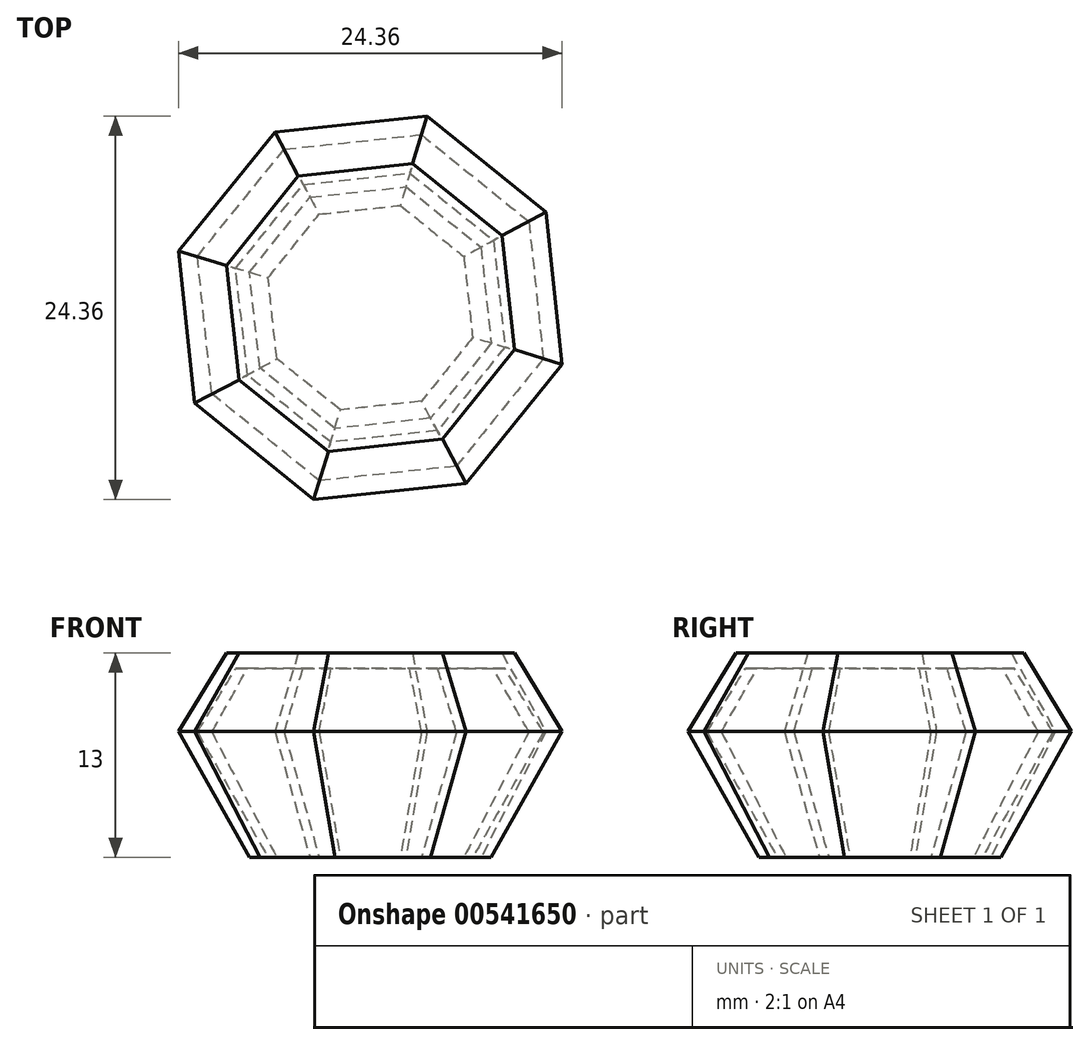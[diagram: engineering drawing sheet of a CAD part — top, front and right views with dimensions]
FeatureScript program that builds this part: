
annotation { "Feature Type Name" : "Feature", "Feature Type Description" : "" }
export const myFeature = defineFeature(function(context is Context, id is Id, definition is map)
    precondition{}
    {
        {
            var Q0;
            Q0=qCreatedBy(makeId("Top.planeOp"),FACE);
            var sketch = newSketch(context, id + "F0", { "sketchPlane" : qUnion([Q0])});
            skCircle(sketch, "E0.cCircle", {"center": v(0, 0) * mm, "radius": 9.53 * mm, "construction": true});
            skLineSegment(sketch, "E0.0", {"start": v(-4.58, 8.35) * mm, "end": v(2.67, 9.14) * mm});
            skLineSegment(sketch, "E0.1", {"start": v(2.67, 9.14) * mm, "end": v(8.35, 4.58) * mm});
            skLineSegment(sketch, "E0.2", {"start": v(8.35, 4.58) * mm, "end": v(9.14, -2.67) * mm});
            skLineSegment(sketch, "E0.3", {"start": v(9.14, -2.67) * mm, "end": v(4.58, -8.35) * mm});
            skLineSegment(sketch, "E0.4", {"start": v(4.58, -8.35) * mm, "end": v(-2.67, -9.14) * mm});
            skLineSegment(sketch, "E0.5", {"start": v(-2.67, -9.14) * mm, "end": v(-8.35, -4.58) * mm});
            skLineSegment(sketch, "E0.6", {"start": v(-8.35, -4.58) * mm, "end": v(-9.14, 2.67) * mm});
            skLineSegment(sketch, "E0.7", {"start": v(-9.14, 2.67) * mm, "end": v(-4.58, 8.35) * mm});
            skSolve(sketch);
        }
        {
            var Q0;
            Q0=qCreatedBy(makeId("Top.planeOp"),FACE);
            cPlane(context, id + "F1", {"entities" : qUnion([Q0]), "cplaneType" : CPlaneType.OFFSET, "offset" : 5 * mm, "oppositeDirection" : true, "width" : 152.4 * mm, "height" : 152.4 * mm});
        }
        {
            var Q0;
            Q0=qCreatedBy(id+"F1.planeOp",FACE);
            var sketch = newSketch(context, id + "F2", { "sketchPlane" : qUnion([Q0])});
            skCircle(sketch, "E1.cCircle", {"center": v(0, 0) * mm, "radius": 12.7 * mm, "construction": true});
            skLineSegment(sketch, "E1.0", {"start": v(-6.06, 11.16) * mm, "end": v(3.6, 12.18) * mm});
            skLineSegment(sketch, "E1.1", {"start": v(3.6, 12.18) * mm, "end": v(11.16, 6.06) * mm});
            skLineSegment(sketch, "E1.2", {"start": v(11.16, 6.06) * mm, "end": v(12.18, -3.6) * mm});
            skLineSegment(sketch, "E1.3", {"start": v(12.18, -3.6) * mm, "end": v(6.06, -11.16) * mm});
            skLineSegment(sketch, "E1.4", {"start": v(6.06, -11.16) * mm, "end": v(-3.6, -12.18) * mm});
            skLineSegment(sketch, "E1.5", {"start": v(-3.6, -12.18) * mm, "end": v(-11.16, -6.06) * mm});
            skLineSegment(sketch, "E1.6", {"start": v(-11.16, -6.06) * mm, "end": v(-12.18, 3.6) * mm});
            skLineSegment(sketch, "E1.7", {"start": v(-12.18, 3.6) * mm, "end": v(-6.06, 11.16) * mm});
            skSolve(sketch);
        }
        {
            var Q0;
            Q0=makeQuery(id+"F0.imprint","IMPRINT",FACE,{"disambiguationData":[TD([[makeQuery(id+"F0.imprint","IMPRINT",EDGE,{"derivedFrom":sQuery(id+"F0.wireOp",EDGE,"E0.0")}),-1.0]])]});
            var Q1;
            Q1=makeQuery(id+"F2.imprint","IMPRINT",FACE,{"disambiguationData":[TD([[makeQuery(id+"F2.imprint","IMPRINT",EDGE,{"derivedFrom":sQuery(id+"F2.wireOp",EDGE,"E1.0")}),-1.0]])]});
            loft(context, id + "F3", {"sheetProfilesArray" : [{ "sheetProfileEntities" : qUnion([Q0]) }, { "sheetProfileEntities" : qUnion([Q1]) }]});
        }
        {
            var Q0;
            Q0=qCreatedBy(id+"F1.planeOp",FACE);
            cPlane(context, id + "F4", {"entities" : qUnion([Q0]), "cplaneType" : CPlaneType.OFFSET, "offset" : 8 * mm, "oppositeDirection" : true, "width" : 152.4 * mm, "height" : 152.4 * mm});
        }
        {
            var Q0;
            Q0=qCreatedBy(id+"F4.planeOp",FACE);
            var sketch = newSketch(context, id + "F5", { "sketchPlane" : qUnion([Q0])});
            skCircle(sketch, "E2.cCircle", {"center": v(0, 0) * mm, "radius": 8 * mm, "construction": true});
            skLineSegment(sketch, "E2.0", {"start": v(-3.84, 7.02) * mm, "end": v(2.25, 7.68) * mm});
            skLineSegment(sketch, "E2.1", {"start": v(2.25, 7.68) * mm, "end": v(7.02, 3.84) * mm});
            skLineSegment(sketch, "E2.2", {"start": v(7.02, 3.84) * mm, "end": v(7.68, -2.25) * mm});
            skLineSegment(sketch, "E2.3", {"start": v(7.68, -2.25) * mm, "end": v(3.84, -7.02) * mm});
            skLineSegment(sketch, "E2.4", {"start": v(3.84, -7.02) * mm, "end": v(-2.25, -7.68) * mm});
            skLineSegment(sketch, "E2.5", {"start": v(-2.25, -7.68) * mm, "end": v(-7.02, -3.84) * mm});
            skLineSegment(sketch, "E2.6", {"start": v(-7.02, -3.84) * mm, "end": v(-7.68, 2.25) * mm});
            skLineSegment(sketch, "E2.7", {"start": v(-7.68, 2.25) * mm, "end": v(-3.84, 7.02) * mm});
            skSolve(sketch);
        }
        {
            var Q1;
            Q1=makeQuery(id+"F3.opLoft","CAP_FACE",FACE,{"disambiguationData":[OSD([makeQuery(id+"F2.imprint","IMPRINT",FACE,{"disambiguationData":[TD([[makeQuery(id+"F2.imprint","IMPRINT",EDGE,{"derivedFrom":sQuery(id+"F2.wireOp",EDGE,"E1.0")}),-1.0]])]})])],"isStart":true});
            var Q2;
            Q2=makeQuery(id+"F5.imprint","IMPRINT",FACE,{"disambiguationData":[TD([[makeQuery(id+"F5.imprint","IMPRINT",EDGE,{"derivedFrom":sQuery(id+"F5.wireOp",EDGE,"E2.0")}),-1.0]])]});
            loft(context, id + "F6", {"operationType" : NewBodyOperationType.ADD, "sheetProfilesArray" : [{ "sheetProfileEntities" : qUnion([Q1]) }, { "sheetProfileEntities" : qUnion([Q2]) }]});
        }
        {
            var Q0;
            Q0=makeQuery(id+"F6.opLoft","CAP_FACE",FACE,{"disambiguationData":[OSD([makeQuery(id+"F5.imprint","IMPRINT",FACE,{"disambiguationData":[TD([[makeQuery(id+"F5.imprint","IMPRINT",EDGE,{"derivedFrom":sQuery(id+"F5.wireOp",EDGE,"E2.0")}),-1.0]])]})])],"isStart":true});
            shell(context, id + "F7", {"entities" : qUnion([Q0]), "thickness" : 1 * mm});
        }
    });
